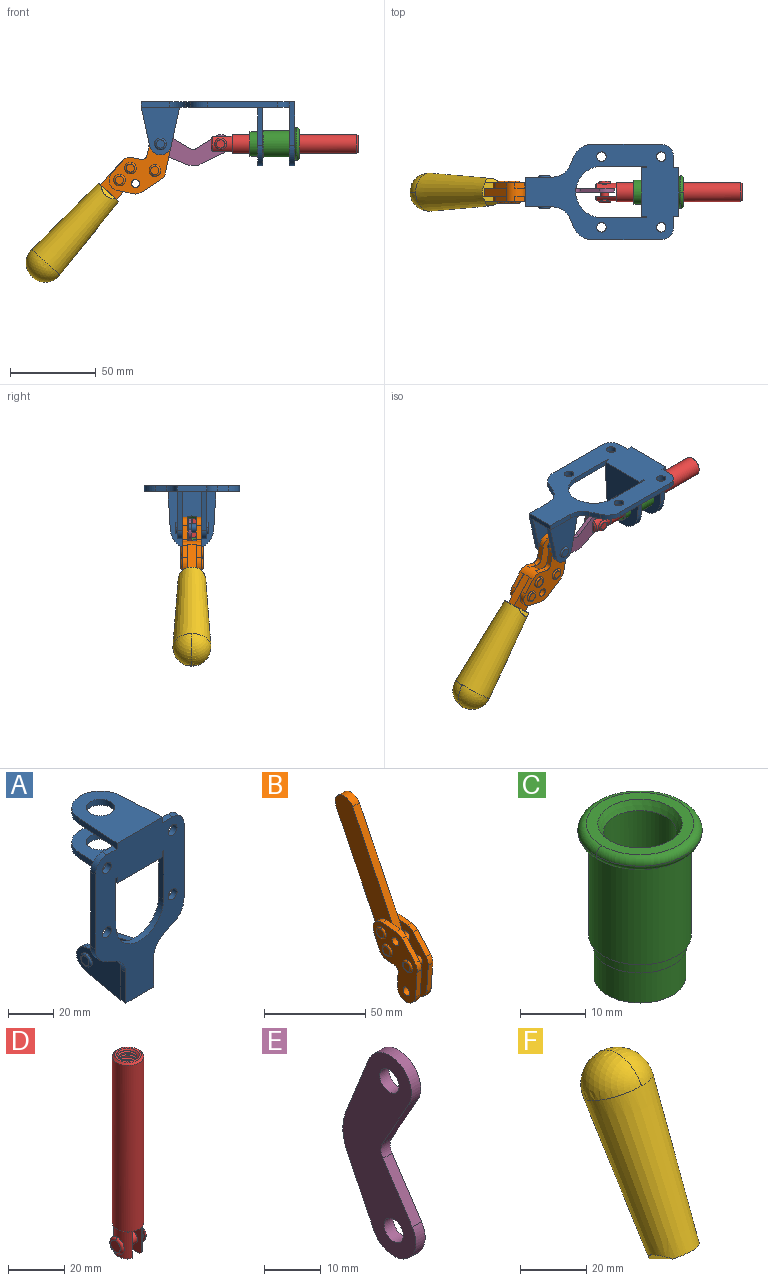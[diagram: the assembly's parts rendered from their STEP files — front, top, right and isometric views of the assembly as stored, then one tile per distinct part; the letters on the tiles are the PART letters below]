
ASSEMBLY  parts=6 mates=5
PART A: 55 faces, bbox 55.7x37.4x89.8 mm
  f0: torus R=2.41mm, axis (-1,0,0), area 15mm2, adj f11,f15,f25
  f1: torus R=2.41mm, axis (-1,0,0), area 15mm2, adj f10,f12,f22
  f2: cylinder r=2.78mm len=5.56mm, axis (0,-1,0), area 54.2mm2, adj f30,f54
  f3: cylinder r=14.99mm len=29.97mm, axis (0,-1,0), area 145.9mm2, adj f30,f49,f53,f54
  f4: cylinder r=2.78mm len=5.56mm, axis (0,-1,0), area 54.2mm2, adj f30,f54
  f5: cylinder r=2.78mm len=5.56mm, axis (0,-1,0), area 54.2mm2, adj f30,f54
  f6: cylinder r=2.78mm len=5.56mm, axis (0,-1,0), area 54.2mm2, adj f30,f54
  f7: cylinder r=6.35mm len=12.7mm, axis (0,0,1), area 123.6mm2, adj f27,f51
  f8: cylinder r=6.35mm len=12.7mm, axis (0,0,-1), area 124.7mm2, adj f21,f35
  f9: cylinder r=2.41mm len=11.18mm, axis (-1,0,0), area 169.4mm2, adj f16,f19
  f10: plane 4.83x4.83mm, normal (1,0,0), area 18.3mm2, adj f1,f12
  f11: plane 4.83x4.83mm, normal (-1,0,0), area 18.3mm2, adj f0,f15
  f12: torus R=2.41mm, axis (-1,0,0), area 15mm2, adj f1,f10,f22
  f13: cylinder r=6.35mm len=12.41mm, axis (1,0,0), area 53.4mm2, adj f18,f19,f22,f23
  f14: cylinder r=6.35mm len=12.41mm, axis (-1,0,0), area 53.4mm2, adj f16,f17,f24,f25
  f15: torus R=2.41mm, axis (-1,0,0), area 15mm2, adj f0,f11,f25
  f16: plane 27.86x22.35mm, normal (1,0,0), area 425.4mm2, adj f9,f14,f17,f24,f30
  f17: plane 22.86x4.97mm, normal (0,0.21,0.98), area 72.5mm2, adj f14,f16,f25,f30
  f18: plane 22.86x4.97mm, normal (0,0.21,0.98), area 72.5mm2, adj f13,f19,f22,f30
  f19: plane 27.86x22.35mm, normal (-1,0,0), area 425.4mm2, adj f9,f13,f18,f23,f30
  f20: cylinder r=12.7mm len=25.35mm, axis (0,0,-1), area 119.8mm2, adj f21,f34,f35,f36
  f21: plane 34.21x28.07mm, normal (0,0,-1), area 702.4mm2, adj f8,f20,f30,f34,f36
  f22: plane 27.96x22.45mm, normal (1,0,0), area 407.2mm2, adj f1,f12,f13,f18,f23,f30,f42,f43
  f23: plane 22.86x4.97mm, normal (0,0.21,-0.98), area 72.5mm2, adj f13,f19,f22,f44
  f24: plane 22.86x4.97mm, normal (0,0.21,-0.98), area 72.5mm2, adj f14,f16,f25,f44
  f25: plane 27.86x22.35mm, normal (-1,0,0), area 407.1mm2, adj f0,f14,f15,f17,f24,f30,f45,f46
  f26: plane 3.1x0.95mm, normal (0,0,-1), area 2.7mm2, adj f30,f49,f50,f54
  f27: plane 34.21x28.07mm, normal (0,0,1), area 702.4mm2, adj f7,f28,f30,f50,f52
  f28: cylinder r=12.7mm len=25.35mm, axis (0,0,1), area 118.8mm2, adj f27,f50,f51,f52
  f29: plane 3.1x0.95mm, normal (0,0,-1), area 2.7mm2, adj f30,f52,f53,f54
  f30: plane 86.54x55.63mm, normal (0,1,0), area 2362.9mm2, adj f2,f3,f4,f5,f6,f16,f17,f18
  f31: plane 40.56x3.1mm, normal (-1,0,0), area 125.7mm2, adj f30,f32,f48,f54
  f32: cylinder r=7.11mm len=7.11mm, axis (0,-1,0), area 34.6mm2, adj f30,f31,f33,f54
  f33: plane 6.67x3.1mm, normal (0,0,1), area 20.4mm2, adj f30,f32,f34,f54
  f34: plane 25.39x3.13mm, normal (-1,0.06,0), area 79.5mm2, adj f20,f21,f33,f35,f54
  f35: plane 37.31x28.45mm, normal (0,0,1), area 789.9mm2, adj f8,f20,f34,f36,f54
  f36: plane 25.39x3.13mm, normal (1,0.06,0), area 79.5mm2, adj f20,f21,f35,f37,f54
  f37: plane 6.67x3.1mm, normal (0,0,1), area 20.4mm2, adj f30,f36,f38,f54
  f38: cylinder r=7.11mm len=7.11mm, axis (0,-1,0), area 34.6mm2, adj f30,f37,f39,f54
  f39: plane 40.56x3.1mm, normal (1,0,0), area 125.7mm2, adj f30,f38,f40,f54
  f40: cylinder r=11.18mm len=10.16mm, axis (0,-1,0), area 39.5mm2, adj f30,f39,f41,f54
  f41: plane 6.09x3.1mm, normal (0.42,0,-0.91), area 20.8mm2, adj f30,f40,f42,f54
  f42: cylinder r=11.18mm len=9.41mm, axis (0,-1,0), area 37.2mm2, adj f22,f30,f41,f43,f54
  f43: plane 16.5x3.1mm, normal (1,0,0), area 51.1mm2, adj f22,f42,f44,f54
  f44: plane 17.37x3.1mm, normal (0,0,-1), area 53.8mm2, adj f23,f24,f30,f43,f45,f54
  f45: plane 16.5x3.1mm, normal (-1,0,0), area 51.1mm2, adj f25,f44,f46,f54
  f46: cylinder r=11.18mm len=9.41mm, axis (0,-1,0), area 37.2mm2, adj f25,f30,f45,f47,f54
  f47: plane 6.09x3.1mm, normal (-0.42,0,-0.91), area 20.8mm2, adj f30,f46,f48,f54
  f48: cylinder r=11.18mm len=10.16mm, axis (0,-1,0), area 39.5mm2, adj f30,f31,f47,f54
  f49: plane 26.54x3.1mm, normal (-1,0,0), area 82.3mm2, adj f3,f26,f30,f54
  f50: plane 25.39x3.1mm, normal (1,0.06,0), area 78.8mm2, adj f26,f27,f28,f51,f54
  f51: plane 37.31x28.45mm, normal (0,0,-1), area 789.9mm2, adj f7,f28,f50,f52,f54
  f52: plane 25.39x3.1mm, normal (-1,0.06,0), area 78.8mm2, adj f27,f28,f29,f51,f54
  f53: plane 26.54x3.1mm, normal (1,0,0), area 82.3mm2, adj f3,f29,f30,f54
  f54: plane 89.66x55.63mm, normal (0,-1,0), area 2678.5mm2, adj f2,f3,f4,f5,f6,f26,f29,f31
PART B: 59 faces, bbox 12.9x60.2x99.6 mm
  f0: torus R=2.39mm, axis (-1,0,0), area 14.9mm2, adj f20,f43,f51
  f1: torus R=2.39mm, axis (-1,0,0), area 14.9mm2, adj f19,f42,f51
  f2: torus R=2.39mm, axis (-1,0,0), area 14.9mm2, adj f18,f35,f51
  f3: torus R=2.39mm, axis (-1,0,0), area 14.9mm2, adj f14,f17,f23
  f4: torus R=2.39mm, axis (-1,0,0), area 14.9mm2, adj f13,f16,f23
  f5: torus R=2.39mm, axis (-1,0,0), area 14.9mm2, adj f12,f15,f23
  f6: cylinder r=2.39mm len=4.78mm, axis (1,0,0), area 46.5mm2, adj f48,f50,f51
  f7: cylinder r=2.39mm len=4.78mm, axis (1,0,0), area 46.5mm2, adj f50,f51
  f8: cylinder r=6.35mm len=12.68mm, axis (1,0,0), area 61.8mm2, adj f38,f39,f50,f51
  f9: cylinder r=2.39mm len=4.78mm, axis (-1,0,0), area 70.5mm2, adj f46,f50
  f10: cylinder r=2.39mm len=4.78mm, axis (-1,0,0), area 46.5mm2, adj f23,f45,f46
  f11: cylinder r=2.39mm len=4.78mm, axis (-1,0,0), area 46.5mm2, adj f23,f46
  f12: plane 4.78x4.78mm, normal (1,0,0), area 17.9mm2, adj f5,f15
  f13: plane 4.78x4.78mm, normal (1,0,0), area 17.9mm2, adj f4,f16
  f14: plane 4.78x4.78mm, normal (1,0,0), area 17.9mm2, adj f3,f17
  f15: torus R=2.39mm, axis (-1,0,0), area 14.9mm2, adj f5,f12,f23
  f16: torus R=2.39mm, axis (-1,0,0), area 14.9mm2, adj f4,f13,f23
  f17: torus R=2.39mm, axis (-1,0,0), area 14.9mm2, adj f3,f14,f23
  f18: plane 4.78x4.78mm, normal (-1,0,0), area 17.9mm2, adj f2,f35
  f19: plane 4.78x4.78mm, normal (-1,0,0), area 17.9mm2, adj f1,f42
  f20: plane 4.78x4.78mm, normal (-1,0,0), area 17.9mm2, adj f0,f43
  f21: plane 2.26x0.2mm, normal (1,0,0), area 0.2mm2, adj f31,f44
  f22: plane 2.26x0.2mm, normal (-1,0,0), area 0.2mm2, adj f41,f44
  f23: plane 39.37x30.77mm, normal (1,0,0), area 565.5mm2, adj f3,f4,f5,f10,f11,f15,f16,f17
  f24: cylinder r=6.1mm len=4.15mm, axis (-1,0,0), area 14.7mm2, adj f23,f25,f32,f46
  f25: plane 10.25x9.01mm, normal (0,-0.75,0.66), area 42.3mm2, adj f23,f24,f26,f46
  f26: cylinder r=6.35mm len=4.64mm, axis (-1,0,0), area 15.6mm2, adj f23,f25,f27,f46
  f27: plane 15.84x3.1mm, normal (0,-1,-0.07), area 49.2mm2, adj f23,f26,f28,f46
  f28: cylinder r=6.35mm len=12.68mm, axis (-1,0,0), area 61.8mm2, adj f23,f27,f29,f46
  f29: plane 8.11x3.1mm, normal (0,1,0.07), area 25.2mm2, adj f23,f28,f30,f46
  f30: cylinder r=3.05mm len=3.25mm, axis (-1,0,0), area 14.8mm2, adj f23,f29,f31,f46
  f31: plane 5.99x3.1mm, normal (0,0.07,-1), area 18.6mm2, adj f21,f23,f30,f44,f46
  f32: plane 9.5x3.1mm, normal (0,-0.07,1), area 29.5mm2, adj f23,f24,f33,f46,f47
  f33: cylinder r=6.1mm len=8.63mm, axis (-1,0,0), area 39.1mm2, adj f23,f32,f34,f47
  f34: plane 8.65x3.96mm, normal (0,0.91,-0.42), area 29.5mm2, adj f23,f33,f44,f47
  f35: torus R=2.39mm, axis (-1,0,0), area 14.9mm2, adj f2,f18,f51
  f36: plane 10.25x9.01mm, normal (0,-0.75,0.66), area 42.3mm2, adj f37,f49,f50,f51
  f37: cylinder r=6.35mm len=4.64mm, axis (1,0,0), area 15.6mm2, adj f36,f38,f50,f51
  f38: plane 15.84x3.1mm, normal (0,-1,-0.07), area 49.2mm2, adj f8,f37,f50,f51
  f39: plane 8.11x3.1mm, normal (0,1,0.07), area 25.2mm2, adj f8,f40,f50,f51
  f40: cylinder r=3.05mm len=3.25mm, axis (1,0,0), area 14.8mm2, adj f39,f41,f50,f51
  f41: plane 5.99x3.1mm, normal (0,0.07,-1), area 18.6mm2, adj f22,f40,f44,f50,f51
  f42: torus R=2.39mm, axis (-1,0,0), area 14.9mm2, adj f1,f19,f51
  f43: torus R=2.39mm, axis (-1,0,0), area 14.9mm2, adj f0,f20,f51
  f44: cylinder r=6.35mm len=12.12mm, axis (-1,0,0), area 128.9mm2, adj f21,f22,f23,f31,f34,f41,f46,f47
  f45: plane 2.65x1.35mm, normal (1,0,0), area 1mm2, adj f10,f55
  f46: plane 39.08x20.42mm, normal (-1,0,0), area 412.5mm2, adj f9,f10,f11,f24,f25,f26,f27,f28
  f47: plane 77.62x39.82mm, normal (1,0,0), area 850mm2, adj f32,f33,f34,f44,f53,f54,f55
  f48: plane 2.65x1.35mm, normal (-1,0,0), area 1mm2, adj f6,f55
  f49: cylinder r=6.1mm len=4.15mm, axis (1,0,0), area 14.7mm2, adj f36,f50,f51,f56
  f50: plane 39.08x20.42mm, normal (1,0,0), area 412.5mm2, adj f6,f7,f8,f9,f36,f37,f38,f39
  f51: plane 39.37x30.77mm, normal (-1,0,0), area 565.5mm2, adj f0,f1,f2,f6,f7,f8,f35,f36
  f52: plane 8.65x3.96mm, normal (0,0.91,-0.42), area 29.5mm2, adj f44,f51,f57,f58
  f53: plane 68.49x33.4mm, normal (0,0.9,-0.44), area 358.1mm2, adj f44,f47,f54,f58
  f54: cylinder r=6.35mm len=12.06mm, axis (1,0,0), area 93.7mm2, adj f47,f53,f55,f58
  f55: plane 68.49x33.4mm, normal (0,-0.9,0.44), area 358.1mm2, adj f44,f45,f46,f47,f48,f50,f54,f58
  f56: plane 9.5x3.1mm, normal (0,-0.07,1), area 29.5mm2, adj f49,f50,f51,f57,f58
  f57: cylinder r=6.1mm len=8.63mm, axis (1,0,0), area 39.1mm2, adj f51,f52,f56,f58
  f58: plane 77.62x39.82mm, normal (-1,0,0), area 850mm2, adj f44,f52,f53,f54,f55,f56,f57
PART C: 15 faces, bbox 20.6x20.6x28.7 mm
  f0: torus R=8.26mm, axis (0,0,1), area 56.8mm2, adj f1,f10,f12
  f1: torus R=8.26mm, axis (0,0,1), area 56.8mm2, adj f0,f6,f13
  f2: cylinder r=5.59mm len=25.91mm, axis (0,0,1), area 909.6mm2, adj f3,f4
  f3: cone r=6.86mm half-angle=45deg, axis (0,0,-1), area 70.2mm2, adj f2,f14
  f4: cone r=6.47mm half-angle=30deg, axis (0,0,1), area 66.7mm2, adj f2,f13
  f5: cylinder r=7.04mm len=14.07mm, axis (0,0,1), area 252.6mm2, adj f11,f14
  f6: torus R=8.26mm, axis (0,0,1), area 56.8mm2, adj f1,f12,f13
  f7: cylinder r=7.16mm len=14.33mm, axis (0,0,1), area 91.5mm2, adj f9,f11
  f8: cylinder r=7.86mm len=18.42mm, axis (0,0,1), area 909.6mm2, adj f9,f10
  f9: plane 15.72x15.72mm, normal (0,0,-1), area 33mm2, adj f7,f8
  f10: plane 16.51x16.51mm, normal (0,0,-1), area 19.9mm2, adj f0,f8,f12
  f11: plane 14.33x14.33mm, normal (0,0,-1), area 5.7mm2, adj f5,f7
  f12: torus R=8.26mm, axis (0,0,1), area 56.8mm2, adj f0,f6,f10
  f13: plane 16.51x16.51mm, normal (0,0,1), area 82.7mm2, adj f1,f4,f6
  f14: plane 14.07x14.07mm, normal (0,0,-1), area 7.8mm2, adj f3,f5
PART D: 48 faces, bbox 12.6x11.1x86.1 mm
  f0: torus R=2.41mm, axis (-1,0,0), area 15mm2, adj f30,f32,f34
  f1: torus R=2.41mm, axis (-1,0,0), area 15mm2, adj f29,f31,f33
  f2: cylinder r=5.54mm len=72.39mm, axis (0,0,1), area 2518.5mm2, adj f3,f4,f42,f43
  f3: cone r=5.54mm half-angle=45deg, axis (0,0,1), area 7.6mm2, adj f2,f5,f41
  f4: cone r=5.54mm half-angle=45deg, axis (0,0,-1), area 34.9mm2, adj f2,f39
  f5: cylinder r=5.08mm len=11.48mm, axis (0,0,1), area 108.3mm2, adj f3,f7,f8,f41
  f6: cylinder r=2.41mm len=4.83mm, axis (-1,0,0), area 71.2mm2, adj f40,f41
  f7: cylinder r=2.41mm len=4.83mm, axis (-1,0,0), area 7.6mm2, adj f5,f34
  f8: cone r=5.08mm half-angle=45deg, axis (0,0,1), area 10.6mm2, adj f5,f37,f41
  f9: cone r=3.98mm half-angle=45deg, axis (0,0,1), area 17.6mm2, adj f27,f39,f45,f46,f47
  f10: cylinder r=2.41mm len=4.83mm, axis (-1,0,0), area 7.6mm2, adj f33,f38
  f11: cylinder r=3.2mm len=6.4mm, axis (0,0,1), area 78.4mm2, adj f12,f28,f44,f45,f47
  f12: cylinder r=3.2mm len=6.4mm, axis (0,0,1), area 10.5mm2, adj f11,f13,f45,f47
  f13: cylinder r=3.2mm len=6.4mm, axis (0,0,1), area 10.5mm2, adj f12,f14,f45,f47
  f14: cylinder r=3.2mm len=6.4mm, axis (0,0,1), area 10.5mm2, adj f13,f15,f45,f47
  f15: cylinder r=3.2mm len=6.4mm, axis (0,0,1), area 10.5mm2, adj f14,f16,f45,f47
  f16: cylinder r=3.2mm len=6.4mm, axis (0,0,1), area 10.5mm2, adj f15,f17,f45,f47
  f17: cylinder r=3.2mm len=6.4mm, axis (0,0,1), area 10.5mm2, adj f16,f18,f45,f47
  f18: cylinder r=3.2mm len=6.4mm, axis (0,0,1), area 10.5mm2, adj f17,f19,f45,f47
  f19: cylinder r=3.2mm len=6.4mm, axis (0,0,1), area 10.5mm2, adj f18,f20,f45,f47
  f20: cylinder r=3.2mm len=6.4mm, axis (0,0,1), area 10.5mm2, adj f19,f21,f45,f47
  f21: cylinder r=3.2mm len=6.4mm, axis (0,0,1), area 10.5mm2, adj f20,f22,f45,f47
  f22: cylinder r=3.2mm len=6.4mm, axis (0,0,1), area 10.5mm2, adj f21,f23,f45,f47
  f23: cylinder r=3.2mm len=6.4mm, axis (0,0,1), area 10.5mm2, adj f22,f24,f45,f47
  f24: cylinder r=3.2mm len=6.4mm, axis (0,0,1), area 10.5mm2, adj f23,f25,f45,f47
  f25: cylinder r=3.2mm len=6.4mm, axis (0,0,1), area 10.5mm2, adj f24,f26,f45,f47
  f26: cylinder r=3.2mm len=6.4mm, axis (0,0,1), area 10.5mm2, adj f25,f27,f45,f47
  f27: cylinder r=3.2mm len=6.4mm, axis (0,0,1), area 7.4mm2, adj f9,f26,f45,f47
  f28: cone r=3.2mm half-angle=60deg, axis (0,0,1), area 37.2mm2, adj f11
  f29: plane 4.83x4.83mm, normal (-1,0,0), area 18.3mm2, adj f1,f31
  f30: plane 4.83x4.83mm, normal (1,0,0), area 18.3mm2, adj f0,f32
  f31: torus R=2.41mm, axis (-1,0,0), area 15mm2, adj f1,f29,f33
  f32: torus R=2.41mm, axis (-1,0,0), area 15mm2, adj f0,f30,f34
  f33: plane 6.83x6.83mm, normal (1,0,0), area 18.3mm2, adj f1,f10,f31
  f34: plane 6.83x6.83mm, normal (-1,0,0), area 18.3mm2, adj f0,f7,f32
  f35: cone r=5.08mm half-angle=45deg, axis (0,0,1), area 10.6mm2, adj f36,f38,f40
  f36: plane 7.25x1.97mm, normal (0,0,-1), area 10mm2, adj f35,f40
  f37: plane 7.25x1.97mm, normal (0,0,-1), area 10mm2, adj f8,f41
  f38: cylinder r=5.08mm len=11.48mm, axis (0,0,1), area 108.3mm2, adj f10,f35,f40,f42
  f39: plane 9.55x9.55mm, normal (0,0,1), area 22mm2, adj f4,f9
  f40: plane 12.76x10.09mm, normal (1,0,0), area 95.7mm2, adj f6,f35,f36,f38,f42,f43
  f41: plane 12.76x10.09mm, normal (-1,0,0), area 95.7mm2, adj f3,f5,f6,f8,f37,f43
  f42: cone r=5.54mm half-angle=45deg, axis (0,0,1), area 7.6mm2, adj f2,f38,f40
  f43: plane 11.07x4.7mm, normal (0,0,-1), area 50.4mm2, adj f2,f40,f41
  f44: plane 0.89x0.62mm, normal (-1,0,0), area 0.3mm2, adj f11,f45,f46,f47
  f45: bspline ~24.8x7.63mm, area 266.6mm2, adj f9,f11,f12,f13,f14,f15,f16,f17
  f46: bspline ~24.87x7.63mm, area 73.6mm2, adj f9,f44,f45,f47
  f47: bspline ~24.98x7.63mm, area 272.5mm2, adj f9,f11,f12,f13,f14,f15,f16,f17
PART E: 12 faces, bbox 2.3x18.2x42.8 mm
  f0: cylinder r=2.4mm len=4.8mm, axis (1,0,0), area 34.9mm2, adj f4,f11
  f1: cylinder r=10.41mm len=8.47mm, axis (1,0,0), area 20.2mm2, adj f4,f9,f10,f11
  f2: cylinder r=3.05mm len=3.16mm, axis (1,0,0), area 7.7mm2, adj f4,f6,f7,f11
  f3: cylinder r=2.4mm len=4.8mm, axis (1,0,0), area 34.9mm2, adj f4,f11
  f4: plane 42.81x18.23mm, normal (-1,0,0), area 414.1mm2, adj f0,f1,f2,f3,f5,f6,f7,f8
  f5: cylinder r=5.54mm len=10.67mm, axis (1,0,0), area 41.8mm2, adj f4,f6,f10,f11
  f6: plane 11.66x6.53mm, normal (0,-0.87,-0.49), area 30.9mm2, adj f2,f4,f5,f11
  f7: plane 11.17x7.33mm, normal (0,-0.84,0.55), area 30.9mm2, adj f2,f4,f8,f11
  f8: cylinder r=5.54mm len=10.51mm, axis (1,0,0), area 41.8mm2, adj f4,f7,f9,f11
  f9: plane 13.67x6.67mm, normal (0,0.9,-0.44), area 35.1mm2, adj f1,f4,f8,f11
  f10: plane 14.1x5.7mm, normal (0,0.93,0.37), area 35.1mm2, adj f1,f4,f5,f11
  f11: plane 42.81x18.23mm, normal (1,0,0), area 414.1mm2, adj f0,f1,f2,f3,f5,f6,f7,f8
PART F: 11 faces, bbox 22.3x42.6x64.5 mm
  f0: sphere r=11.13mm, area 411.4mm2, adj f1,f8
  f1: cone r=11.11mm half-angle=3.3deg, axis (0,0.44,0.9), area 3251.8mm2, adj f0,f7,f8,f9,f10
  f2: cylinder r=6.16mm len=11.7mm, axis (1,0,0), area 89.5mm2, adj f3,f4,f5,f6
  f3: plane 60.23x36.75mm, normal (-1,0,0), area 763.6mm2, adj f2,f4,f6,f10
  f4: plane 51.37x25.05mm, normal (0,0.9,-0.44), area 264.2mm2, adj f2,f3,f5,f10
  f5: plane 60.23x36.75mm, normal (1,0,0), area 763.6mm2, adj f2,f4,f6,f10
  f6: plane 51.37x25.05mm, normal (0,-0.9,0.44), area 264.2mm2, adj f2,f3,f5,f10
  f7: plane 9.95x5.95mm, normal (0.71,-0.31,-0.64), area 25.8mm2, adj f1,f10
  f8: sphere r=11.13mm, area 411.4mm2, adj f0,f1
  f9: plane 9.95x5.95mm, normal (-0.71,-0.31,-0.64), area 25.8mm2, adj f1,f10
  f10: plane 14.27x11.38mm, normal (0,-0.44,-0.9), area 106.7mm2, adj f1,f3,f4,f5,f6,f7,f9
PLACE A rot(axis=(-0.58,0.58,-0.58),120deg) t=(0,0,0)mm fixed
PLACE B rot(axis=(0.7,-0.7,-0.1),168.8deg) t=(-17.24,0,-62.23)mm
PLACE C rot(axis=(0.71,0,0.71),180deg) t=(0,24.61,-24.61)mm
PLACE D rot(axis=(-0.58,0.58,-0.58),120deg) t=(-12.39,0,0)mm
PLACE E rot(axis=(-0.58,-0.58,0.58),120deg) t=(-13.17,1.16,-1.11)mm
PLACE F rot(axis=(0.7,-0.7,-0.1),168.8deg) t=(-17.24,0.04,-62.23)mm
MATE fastened C.f2 <-> A.f7  axis (-1,0,0) through (46.39,0,-24.61)mm
MATE revolute A.f0 <-> B.f7  axis (0,1,0) through (-32.09,0,-24.61)mm
MATE slider A.f7 <-> D.f2  axis (1,0,0) through (46.39,0,-24.61)mm
MATE revolute D.f6 <-> E.f3  axis (0,1,0) through (3.09,0,-24.61)mm
MATE fastened F.f2 <-> B.f54  axis (0,-1,0) through (-100.58,2.35,-95.4)mm
